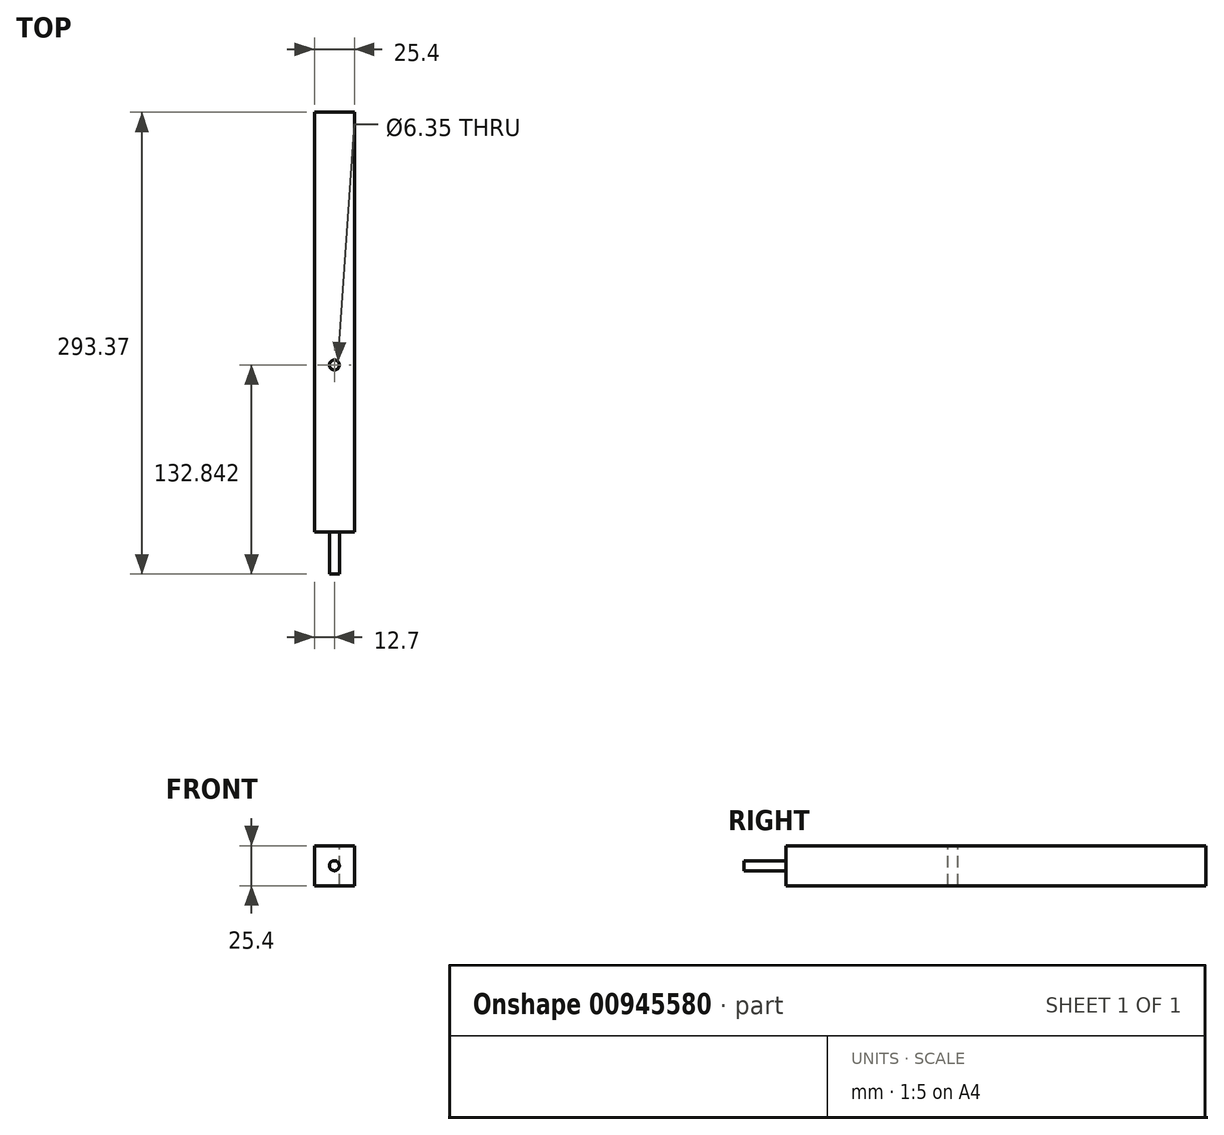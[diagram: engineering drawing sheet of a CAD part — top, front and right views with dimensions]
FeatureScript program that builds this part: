
annotation { "Feature Type Name" : "Feature", "Feature Type Description" : "" }
export const myFeature = defineFeature(function(context is Context, id is Id, definition is map)
    precondition{}
    {
        {
            var Q0;
            Q0=qCreatedBy(makeId("Front.planeOp"),FACE);
            var sketch = newSketch(context, id + "F0", { "sketchPlane" : qUnion([Q0])});
            skLineSegment(sketch, "E0.bottom", {"start": v(12.7, -12.7) * mm, "end": v(-12.7, -12.7) * mm});
            skLineSegment(sketch, "E0.top", {"start": v(12.7, 12.7) * mm, "end": v(-12.7, 12.7) * mm});
            skLineSegment(sketch, "E0.left", {"start": v(12.7, -12.7) * mm, "end": v(12.7, 12.7) * mm});
            skLineSegment(sketch, "E0.right", {"start": v(-12.7, -12.7) * mm, "end": v(-12.7, 12.7) * mm});
            skPoint(sketch, "E0.middle", {"position": v(0, 0) * mm});
            skSolve(sketch);
        }
        {
            var Q0;
            Q0=qSketchRegion(id+"F0",true);
            extrude(context, id + "F1", {"entities" : qUnion([Q0]), "oppositeDirection" : true, "depth" : 266.7 * mm, "offsetDistance" : 25 * mm});
        }
        {
            var Q0;
            Q0=makeQuery(id+"F1.opExtrude","CAP_FACE",FACE,{"disambiguationData":[OSD([sQuery(id+"F0.wireOp",EDGE,"E0.bottom"),sQuery(id+"F0.wireOp",EDGE,"E0.top"),sQuery(id+"F0.wireOp",EDGE,"E0.left"),sQuery(id+"F0.wireOp",EDGE,"E0.right")])],"isStart":true});
            var sketch = newSketch(context, id + "F2", { "sketchPlane" : qUnion([Q0])});
            skCircle(sketch, "E1", {"center": v(0, 0) * mm, "radius": 3.18 * mm});
            skSolve(sketch);
        }
        {
            var Q0;
            Q0=qSketchRegion(id+"F2",true);
            extrude(context, id + "F3", {"entities" : qUnion([Q0]), "operationType" : NewBodyOperationType.ADD, "depth" : 26.67 * mm, "offsetDistance" : 25 * mm});
        }
        {
            var Q0;
            Q0=makeQuery(id+"F1.opExtrude","SWEPT_FACE",FACE,{"disambiguationData":[OSD([sQuery(id+"F0.wireOp",EDGE,"E0.top")])]});
            var sketch = newSketch(context, id + "F4", { "sketchPlane" : qUnion([Q0])});
            skCircle(sketch, "E2", {"center": v(0, 106.17) * mm, "radius": 3.18 * mm});
            skSolve(sketch);
        }
        {
            var Q0;
            Q0=qSketchRegion(id+"F4",true);
            var Q1;
            Q1=makeQuery(id+"F1.opExtrude","SWEPT_FACE",FACE,{"disambiguationData":[OSD([sQuery(id+"F0.wireOp",EDGE,"E0.bottom")])]});
            extrude(context, id + "F5", {"entities" : qUnion([Q0]), "operationType" : NewBodyOperationType.REMOVE, "endBound" : BoundingType.UP_TO_SURFACE, "oppositeDirection" : true, "depth" : 25 * mm, "endBoundEntityFace" : qUnion([Q1]), "offsetDistance" : 25 * mm});
        }
    });
